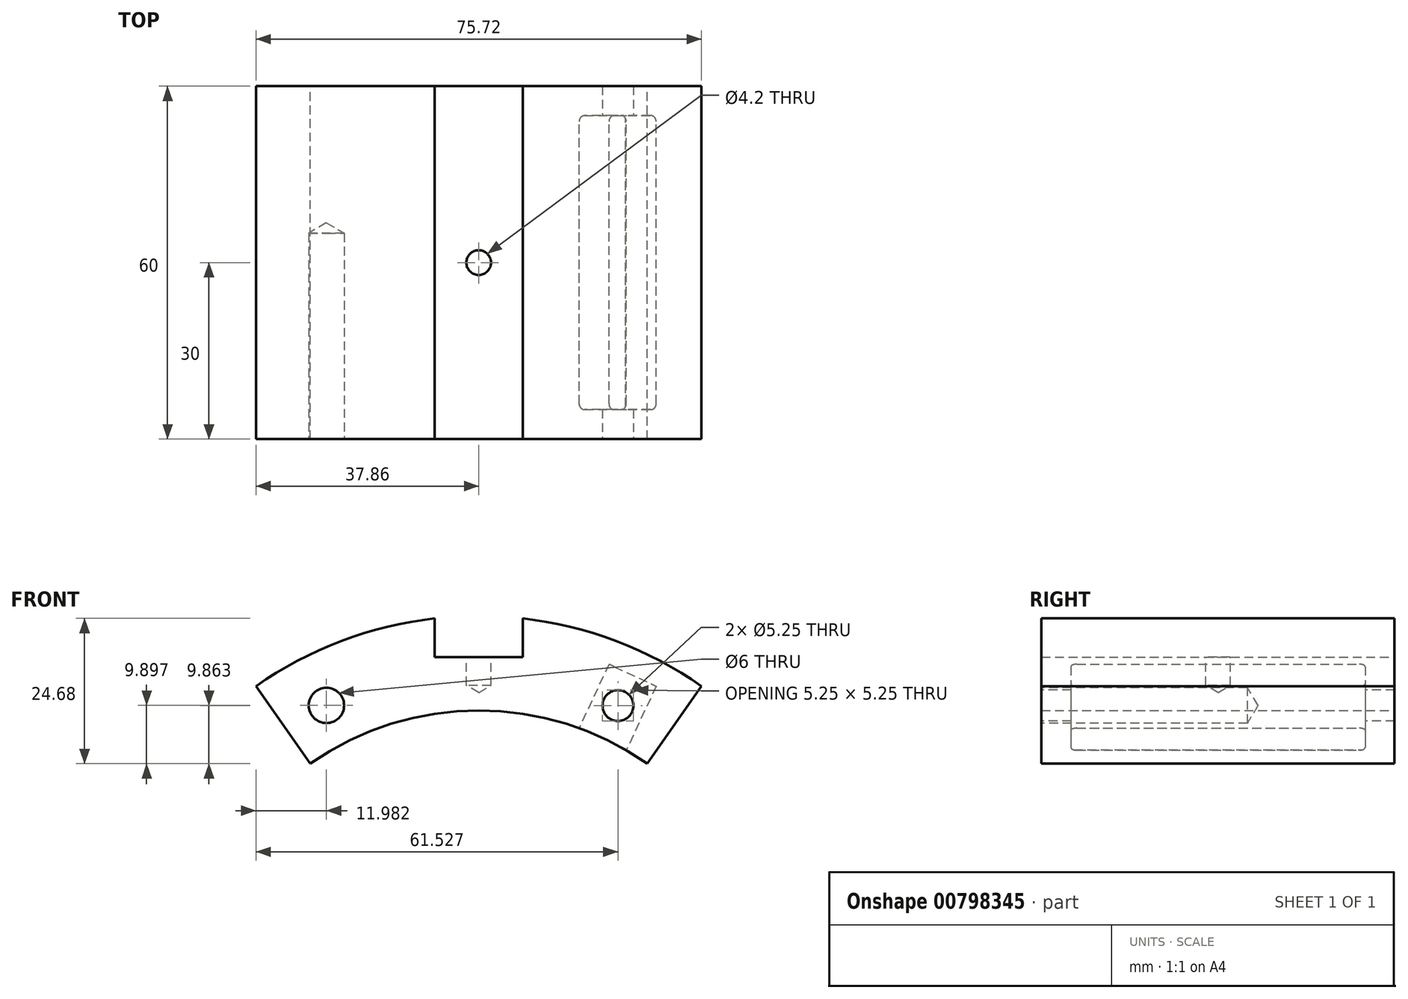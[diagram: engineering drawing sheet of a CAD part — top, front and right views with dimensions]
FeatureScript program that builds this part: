
annotation { "Feature Type Name" : "Feature", "Feature Type Description" : "" }
export const myFeature = defineFeature(function(context is Context, id is Id, definition is map)
    precondition{}
    {
        {
            assignVariable(context, id + "F0", {"name" : "LargoPAD", "anyValue" : 60});
        }
        {
            assignVariable(context, id + "F1", {"name" : "DepthLEG", "anyValue" : 12});
        }
        {
            var Q0;
            Q0=qCreatedBy(makeId("Front.planeOp"),FACE);
            var sketch = newSketch(context, id + "F2", { "sketchPlane" : qUnion([Q0])});
            skArc(sketch, "E0", {"start": v(28.63, 40.9) * mm, "mid": v(0, 49.92) * mm, "end": v(-28.63, 40.9) * mm});
            skLineSegment(sketch, "E1", {"start": v(0, 0) * mm, "end": v(28.63, 40.9) * mm});
            skLineSegment(sketch, "E2", {"start": v(0, 0) * mm, "end": v(-28.63, 40.9) * mm});
            skArc(sketch, "E3", {"start": v(37.86, 54.06) * mm, "mid": v(0, 66) * mm, "end": v(-37.86, 54.06) * mm});
            skLineSegment(sketch, "E4", {"start": v(0, 0) * mm, "end": v(37.86, 54.06) * mm});
            skLineSegment(sketch, "E5", {"start": v(0, 0) * mm, "end": v(-37.86, 54.06) * mm});
            skPoint(sketch, "E6", {"position": v(0, 59) * mm});
            skLineSegment(sketch, "E7", {"start": v(0, 59) * mm, "end": v(7.5, 59) * mm});
            skLineSegment(sketch, "E8.MirrorCS", {"start": v(0, 59) * mm, "end": v(-7.5, 59) * mm});
            skLineSegment(sketch, "E9", {"start": v(7.5, 59) * mm, "end": v(7.5, 65.57) * mm});
            skLineSegment(sketch, "E10.MirrorCS", {"start": v(-7.5, 59) * mm, "end": v(-7.5, 65.57) * mm});
            skSolve(sketch);
        }
        {
            var Q0;
            {var subQ7=sQuery(id+"F2.wireOp",EDGE,"E0");Q0=makeQuery(id+"F2.imprint","IMPRINT",FACE,{"disambiguationData":[TD([[makeQuery(id+"F2.imprint","IMPRINT",EDGE,{"derivedFrom":subQ7}),-1.0]])]});}
            var Q1;
            Q1 = qSketchRegion(id + "F4", true);
            extrude(context, id + "F3", {"entities" : qUnion([Q0, Q1]), "depth" : (getVariable(context, 'LargoPAD')) * mm, "offsetDistance" : 25 * mm});
        }
        {
            var Q0;
            Q0=makeQuery(id+"F3.opExtrude","SWEPT_FACE",FACE,{"disambiguationData":[OSD([sQuery(id+"F2.wireOp",EDGE,"E8.MirrorCS"),sQuery(id+"F2.wireOp",EDGE,"E7")])]});
            var sketch = newSketch(context, id + "F4", { "sketchPlane" : qUnion([Q0])});
            skPoint(sketch, "E11", {"position": v(0, -30) * mm});
            skCircle(sketch, "E12", {"center": v(0, -30) * mm, "radius": 2.5 * mm});
            skSolve(sketch);
        }
        {
            var Q0;
            Q0=makeQuery(id+"F3.opExtrude","CAP_FACE",FACE,{"disambiguationData":[OSD([sQuery(id+"F2.wireOp",EDGE,"E0"),sQuery(id+"F2.wireOp",EDGE,"E3"),sQuery(id+"F2.wireOp",EDGE,"E4"),sQuery(id+"F2.wireOp",EDGE,"E5"),sQuery(id+"F2.wireOp",EDGE,"E8.MirrorCS"),sQuery(id+"F2.wireOp",EDGE,"E7"),sQuery(id+"F2.wireOp",EDGE,"E9"),sQuery(id+"F2.wireOp",EDGE,"E10.MirrorCS")])],"isStart":false});
            var sketch = newSketch(context, id + "F5", { "sketchPlane" : qUnion([Q0])});
            skLineSegment(sketch, "E13", {"start": v(0, 0) * mm, "end": v(33, 57.16) * mm});
            skLineSegment(sketch, "E14", {"start": v(0, 0) * mm, "end": v(22.57, 62.02) * mm});
            skLineSegment(sketch, "E15", {"start": v(24.96, 43.23) * mm, "end": v(17.07, 46.91) * mm});
            skPoint(sketch, "E16", {"position": v(17.07, 46.91) * mm});
            skPoint(sketch, "E17", {"position": v(24.96, 43.23) * mm});
            skLineSegment(sketch, "E18", {"start": v(24.96, 43.23) * mm, "end": v(30.03, 54.11) * mm});
            skLineSegment(sketch, "E19", {"start": v(17.07, 46.91) * mm, "end": v(22.15, 57.79) * mm});
            skLineSegment(sketch, "E20", {"start": v(30.03, 54.11) * mm, "end": v(22.15, 57.79) * mm});
            skLineSegment(sketch, "E21", {"start": v(0, 0) * mm, "end": v(23.67, 50.75) * mm});
            skSolve(sketch);
        }
        {
            var Q0;
            Q0=sQuery(id+"F5.wireOp",EDGE,"E15");
            cPlane(context, id + "F6", {"entities" : qUnion([Q0]), "cplaneType" : CPlaneType.LINE_ANGLE, "offset" : 25 * mm, "angle" : 90 * degree, "width" : 150 * mm, "height" : 150 * mm});
        }
        {
            var Q0;
            Q0=qCreatedBy(id+"F6.planeOp",FACE);
            var sketch = newSketch(context, id + "F7", { "sketchPlane" : qUnion([Q0])});
            skLineSegment(sketch, "E22", {"start": v(0, -60) * mm, "end": v(0, 0) * mm});
            skPoint(sketch, "E23", {"position": v(0, -55) * mm});
            skPoint(sketch, "E24", {"position": v(0, -5) * mm});
            skLineSegment(sketch, "E25", {"start": v(-4.36, -54) * mm, "end": v(-4.36, -6) * mm});
            skLineSegment(sketch, "E26", {"start": v(0, -60) * mm, "end": v(4.3, -60) * mm});
            skLineSegment(sketch, "E27", {"start": v(4.49, -54) * mm, "end": v(4.49, -6) * mm});
            skLineSegment(sketch, "E28", {"start": v(0, -55) * mm, "end": v(-3.36, -55) * mm});
            skLineSegment(sketch, "E29", {"start": v(0, -55) * mm, "end": v(3.49, -55) * mm});
            skLineSegment(sketch, "E30", {"start": v(0, -5) * mm, "end": v(-3.36, -5) * mm});
            skLineSegment(sketch, "E31", {"start": v(0, -5) * mm, "end": v(3.49, -5) * mm});
            skPoint(sketch, "E32.newPointB", {"position": v(4.49, -64.81) * mm});
            skArc(sketch, "E32.filletArc", {"start": v(3.49, -55) * mm, "mid": v(4.2, -54.7) * mm, "end": v(4.49, -54) * mm});
            skPoint(sketch, "E33.newPointB", {"position": v(-4.36, -60) * mm});
            skArc(sketch, "E33.filletArc", {"start": v(-4.36, -54) * mm, "mid": v(-4.07, -54.7) * mm, "end": v(-3.36, -55) * mm});
            skPoint(sketch, "E34.newPointB", {"position": v(4.49, 35.19) * mm});
            skArc(sketch, "E34.filletArc", {"start": v(4.49, -6) * mm, "mid": v(4.2, -5.3) * mm, "end": v(3.49, -5) * mm});
            skPoint(sketch, "E35.newPointB", {"position": v(-4.36, 40) * mm});
            skArc(sketch, "E35.filletArc", {"start": v(-3.36, -5) * mm, "mid": v(-4.07, -5.3) * mm, "end": v(-4.36, -6) * mm});
            skSolve(sketch);
        }
        {
            var Q0;
            Q0=makeQuery(id+"F3.opExtrude","CAP_FACE",FACE,{"disambiguationData":[OSD([sQuery(id+"F2.wireOp",EDGE,"E0"),sQuery(id+"F2.wireOp",EDGE,"E3"),sQuery(id+"F2.wireOp",EDGE,"E4"),sQuery(id+"F2.wireOp",EDGE,"E5"),sQuery(id+"F2.wireOp",EDGE,"E8.MirrorCS"),sQuery(id+"F2.wireOp",EDGE,"E7"),sQuery(id+"F2.wireOp",EDGE,"E9"),sQuery(id+"F2.wireOp",EDGE,"E10.MirrorCS")])],"isStart":false});
            var sketch = newSketch(context, id + "F8", { "sketchPlane" : qUnion([Q0])});
            skLineSegment(sketch, "E36", {"start": v(0, 0) * mm, "end": v(-25.88, 50.79) * mm});
            skCircle(sketch, "E37", {"center": v(-25.88, 50.79) * mm, "radius": 3 * mm});
            skSolve(sketch);
        }
        {
            var Q0;
            Q0=sQuery(id+"F8.wireOp",VERTEX,"E36.end");
            var Q1;
            Q1=makeQuery(id+"F3.opExtrude","SWEPT_BODY",BODY,{"disambiguationData":[OSD([sQuery(id+"F2.wireOp",EDGE,"E0"),sQuery(id+"F2.wireOp",EDGE,"E3"),sQuery(id+"F2.wireOp",EDGE,"E4"),sQuery(id+"F2.wireOp",EDGE,"E5"),sQuery(id+"F2.wireOp",EDGE,"E8.MirrorCS"),sQuery(id+"F2.wireOp",EDGE,"E7"),sQuery(id+"F2.wireOp",EDGE,"E9"),sQuery(id+"F2.wireOp",EDGE,"E10.MirrorCS")])]});
            hole(context, id + "F9", {"style" : HoleStyle.SIMPLE, "endStyle" : HoleEndStyle.BLIND, "standardTappedOrClearance" : lookupTablePath({ "standard" : "ISO", "size" : "6", "type" : "Drilled" }), "standardBlindInLast" : lookupTablePath({ "standard" : "ISO", "size" : "6", "type" : "Drilled" }), "holeDiameter" : 6 * mm, "majorDiameter" : 5 * mm, "holeDepth" : 35 * mm, "isTappedThrough" : true, "tappedDepth" : 12 * mm, "tapClearance" : 3, "startFromSketch" : true, "locations" : qUnion([Q0]), "scope" : qUnion([Q1])});
        }
        {
            var Q0;
            Q0=sQuery(id+"F4.wireOp",VERTEX,"E11");
            var Q1;
            Q1=makeQuery(id+"F3.opExtrude","SWEPT_BODY",BODY,{"disambiguationData":[OSD([sQuery(id+"F2.wireOp",EDGE,"E0"),sQuery(id+"F2.wireOp",EDGE,"E3"),sQuery(id+"F2.wireOp",EDGE,"E4"),sQuery(id+"F2.wireOp",EDGE,"E5"),sQuery(id+"F2.wireOp",EDGE,"E8.MirrorCS"),sQuery(id+"F2.wireOp",EDGE,"E7"),sQuery(id+"F2.wireOp",EDGE,"E9"),sQuery(id+"F2.wireOp",EDGE,"E10.MirrorCS")])]});
            hole(context, id + "F10", {"style" : HoleStyle.SIMPLE, "endStyle" : HoleEndStyle.BLIND, "standardTappedOrClearance" : lookupTablePath({ "standard" : "ISO", "engagement" : "75%", "pitch" : "0.8 mm", "size" : "M5", "type" : "Tapped" }), "standardBlindInLast" : lookupTablePath({ "standard" : "ISO", "engagement" : "75%", "pitch" : "0.8 mm", "size" : "M5", "type" : "Tapped" }), "holeDiameter" : 4.2 * mm, "majorDiameter" : 5 * mm, "showTappedDepth" : true, "holeDepth" : 4.8 * mm, "isTappedThrough" : true, "tappedDepth" : 4 * mm, "tapClearance" : 1, "startFromSketch" : true, "locations" : qUnion([Q0]), "scope" : qUnion([Q1])});
        }
        {
            var Q0;
            Q0=makeQuery(id+"F7.imprint","IMPRINT",FACE,{"disambiguationData":[TD([[makeQuery(id+"F7.imprint","IMPRINT",EDGE,{"derivedFrom":sQuery(id+"F7.wireOp",EDGE,"E27")}),1.0]])]});
            var Q1;
            Q1=makeQuery(id+"F7.imprint","IMPRINT",FACE,{"disambiguationData":[TD([[makeQuery(id+"F7.imprint","IMPRINT",EDGE,{"derivedFrom":sQuery(id+"F7.wireOp",EDGE,"E25")}),-1.0]])]});
            var Q2;
            Q2=sQuery(id+"F7.wireOp",EDGE,"E27");
            var Q3;
            Q3=sQuery(id+"F7.wireOp",EDGE,"E32.filletArc");
            var Q4;
            Q4=sQuery(id+"F7.wireOp",EDGE,"E29");
            var Q5;
            Q5=sQuery(id+"F7.wireOp",EDGE,"E28");
            var Q6;
            Q6=sQuery(id+"F7.wireOp",EDGE,"E33.filletArc");
            var Q7;
            Q7=sQuery(id+"F7.wireOp",EDGE,"E25");
            var Q8;
            Q8=sQuery(id+"F7.wireOp",EDGE,"E35.filletArc");
            var Q9;
            Q9=sQuery(id+"F7.wireOp",EDGE,"E30");
            var Q10;
            Q10=sQuery(id+"F7.wireOp",EDGE,"E31");
            var Q11;
            Q11=sQuery(id+"F7.wireOp",EDGE,"E34.filletArc");
            extrude(context, id + "F11", {"entities" : qUnion([Q0, Q1]), "operationType" : NewBodyOperationType.REMOVE, "surfaceOperationType" : NewSurfaceOperationType.ADD, "surfaceEntities" : qUnion([Q2, Q3, Q4, Q5, Q6, Q7, Q8, Q9, Q10, Q11]), "depth" : (getVariable(context, 'DepthLEG')) * mm, "offsetDistance" : 25 * mm});
        }
        {
            var Q0;
            Q0=sQuery(id+"F5.wireOp",VERTEX,"E21.end");
            var Q1;
            Q1=makeQuery(id+"F3.opExtrude","SWEPT_BODY",BODY,{"disambiguationData":[OSD([sQuery(id+"F2.wireOp",EDGE,"E0"),sQuery(id+"F2.wireOp",EDGE,"E3"),sQuery(id+"F2.wireOp",EDGE,"E4"),sQuery(id+"F2.wireOp",EDGE,"E5"),sQuery(id+"F2.wireOp",EDGE,"E8.MirrorCS"),sQuery(id+"F2.wireOp",EDGE,"E7"),sQuery(id+"F2.wireOp",EDGE,"E9"),sQuery(id+"F2.wireOp",EDGE,"E10.MirrorCS")])]});
            hole(context, id + "F12", {"style" : HoleStyle.SIMPLE, "endStyle" : HoleEndStyle.THROUGH, "standardTappedOrClearance" : lookupTablePath({ "standard" : "ISO", "engagement" : "75%", "pitch" : "0.75 mm", "size" : "M6", "type" : "Tapped" }), "standardBlindInLast" : lookupTablePath({ "standard" : "ISO", "engagement" : "75%", "pitch" : "0.75 mm", "size" : "M6", "type" : "Tapped" }), "holeDiameter" : 5.25 * mm, "majorDiameter" : 6 * mm, "showTappedDepth" : true, "isTappedThrough" : true, "tappedDepth" : 2.6 * mm, "tapClearance" : 3, "startFromSketch" : true, "locations" : qUnion([Q0]), "scope" : qUnion([Q1])});
        }
        {
            var Q0;
            Q0=makeQuery(id+"F3.opExtrude","CAP_FACE",FACE,{"disambiguationData":[OSD([sQuery(id+"F2.wireOp",EDGE,"E0"),sQuery(id+"F2.wireOp",EDGE,"E3"),sQuery(id+"F2.wireOp",EDGE,"E4"),sQuery(id+"F2.wireOp",EDGE,"E5"),sQuery(id+"F2.wireOp",EDGE,"E8.MirrorCS"),sQuery(id+"F2.wireOp",EDGE,"E7"),sQuery(id+"F2.wireOp",EDGE,"E9"),sQuery(id+"F2.wireOp",EDGE,"E10.MirrorCS")])],"isStart":true});
            var sketch = newSketch(context, id + "F13", { "sketchPlane" : qUnion([Q0])});
            skLineSegment(sketch, "E38", {"start": v(0, 0) * mm, "end": v(-23.67, 50.75) * mm});
            skSolve(sketch);
        }
        {
            var Q0;
            Q0=sQuery(id+"F13.wireOp",VERTEX,"E38.end");
            var Q1;
            Q1=makeQuery(id+"F3.opExtrude","SWEPT_BODY",BODY,{"disambiguationData":[OSD([sQuery(id+"F2.wireOp",EDGE,"E0"),sQuery(id+"F2.wireOp",EDGE,"E3"),sQuery(id+"F2.wireOp",EDGE,"E4"),sQuery(id+"F2.wireOp",EDGE,"E5"),sQuery(id+"F2.wireOp",EDGE,"E8.MirrorCS"),sQuery(id+"F2.wireOp",EDGE,"E7"),sQuery(id+"F2.wireOp",EDGE,"E9"),sQuery(id+"F2.wireOp",EDGE,"E10.MirrorCS")])]});
            hole(context, id + "F14", {"style" : HoleStyle.SIMPLE, "endStyle" : HoleEndStyle.BLIND, "standardTappedOrClearance" : lookupTablePath({ "standard" : "ISO", "engagement" : "75%", "pitch" : "0.75 mm", "size" : "M6", "type" : "Tapped" }), "standardBlindInLast" : lookupTablePath({ "standard" : "ISO", "engagement" : "75%", "pitch" : "0.75 mm", "size" : "M6", "type" : "Tapped" }), "holeDiameter" : 5.25 * mm, "majorDiameter" : 6 * mm, "showTappedDepth" : true, "holeDepth" : 4.85 * mm, "isTappedThrough" : true, "tappedDepth" : 2.6 * mm, "tapClearance" : 3, "startFromSketch" : true, "locations" : qUnion([Q0]), "scope" : qUnion([Q1])});
        }
    });
